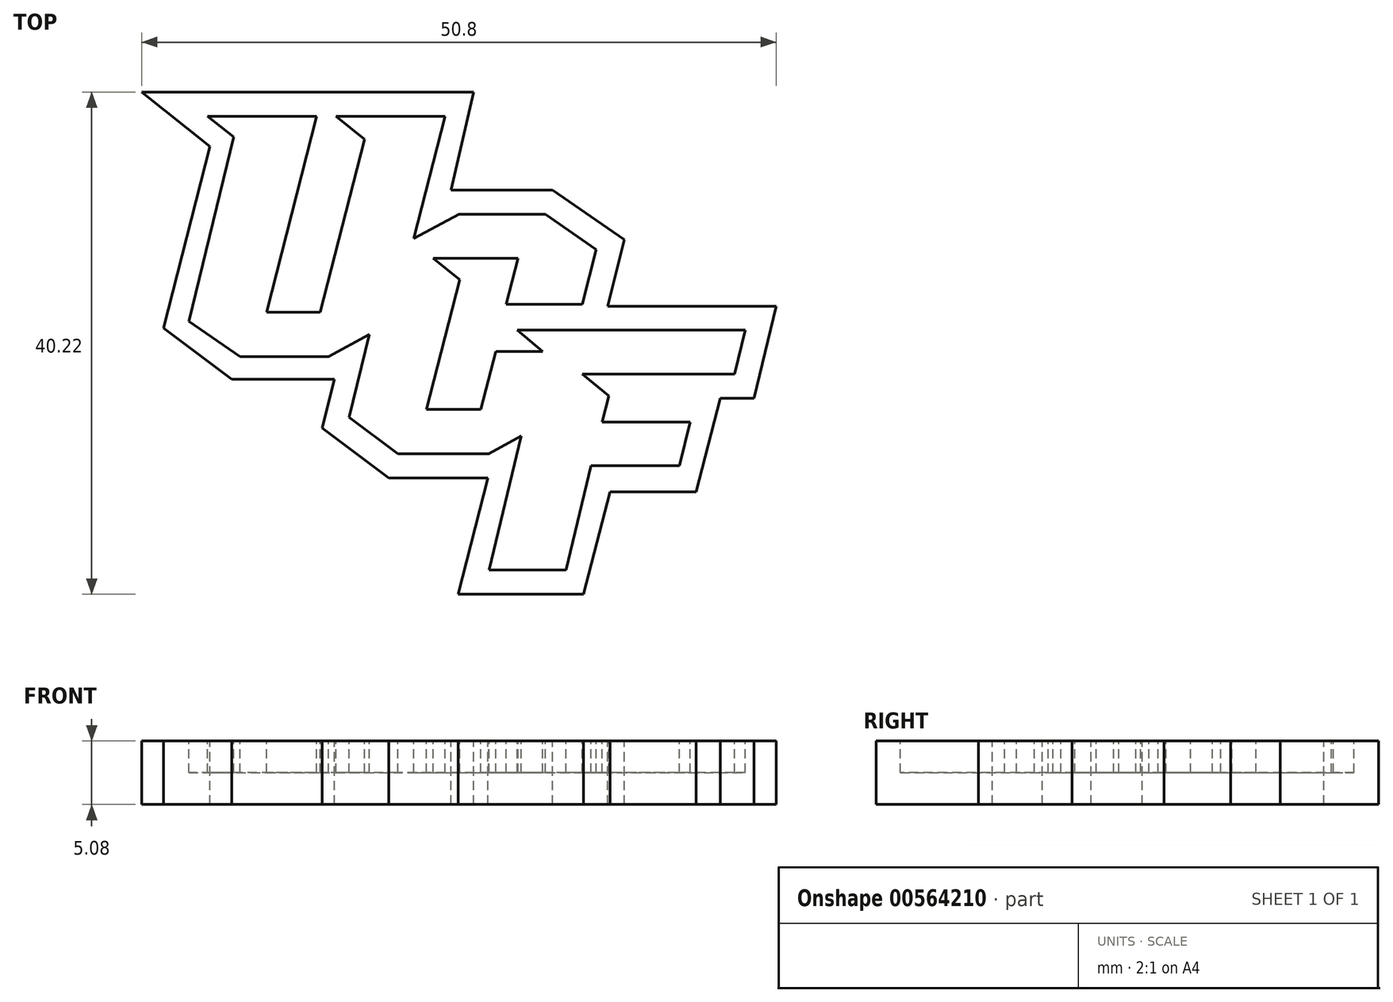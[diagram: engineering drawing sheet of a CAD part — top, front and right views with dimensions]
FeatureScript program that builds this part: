
annotation { "Feature Type Name" : "Feature", "Feature Type Description" : "" }
export const myFeature = defineFeature(function(context is Context, id is Id, definition is map)
    precondition{}
    {
        {
            var Q0;
            Q0=qCreatedBy(makeId("Top.planeOp"),FACE);
            var sketch = newSketch(context, id + "F0", { "sketchPlane" : qUnion([Q0])});
            skLineSegment(sketch, "E0", {"start": v(-24.4, 19.25) * mm, "end": v(2.19, 19.25) * mm});
            skLineSegment(sketch, "E1", {"start": v(2.19, 19.25) * mm, "end": v(0.35, 11.38) * mm});
            skLineSegment(sketch, "E2", {"start": v(0.35, 11.38) * mm, "end": v(8.5, 11.38) * mm});
            skLineSegment(sketch, "E3", {"start": v(8.5, 11.38) * mm, "end": v(14.26, 7.42) * mm});
            skLineSegment(sketch, "E4", {"start": v(14.26, 7.42) * mm, "end": v(12.9, 2.1) * mm});
            skLineSegment(sketch, "E5", {"start": v(12.9, 2.1) * mm, "end": v(26.4, 2.1) * mm});
            skLineSegment(sketch, "E6", {"start": v(26.4, 2.1) * mm, "end": v(24.63, -5.27) * mm});
            skLineSegment(sketch, "E7", {"start": v(24.63, -5.27) * mm, "end": v(21.92, -5.27) * mm});
            skLineSegment(sketch, "E8", {"start": v(21.92, -5.27) * mm, "end": v(20, -12.77) * mm});
            skLineSegment(sketch, "E9", {"start": v(20, -12.77) * mm, "end": v(13.09, -12.77) * mm});
            skLineSegment(sketch, "E10", {"start": v(13.09, -12.77) * mm, "end": v(10.99, -20.97) * mm});
            skLineSegment(sketch, "E11", {"start": v(10.99, -20.97) * mm, "end": v(0.94, -20.97) * mm});
            skLineSegment(sketch, "E12", {"start": v(0.94, -20.97) * mm, "end": v(3.33, -11.66) * mm});
            skLineSegment(sketch, "E13", {"start": v(3.33, -11.66) * mm, "end": v(-4.63, -11.66) * mm});
            skLineSegment(sketch, "E14", {"start": v(-4.63, -11.66) * mm, "end": v(-9.96, -7.66) * mm});
            skLineSegment(sketch, "E15", {"start": v(-9.96, -7.66) * mm, "end": v(-8.96, -3.76) * mm});
            skLineSegment(sketch, "E16", {"start": v(-8.96, -3.76) * mm, "end": v(-17.19, -3.76) * mm});
            skLineSegment(sketch, "E17", {"start": v(-17.19, -3.76) * mm, "end": v(-22.66, 0.35) * mm});
            skLineSegment(sketch, "E18", {"start": v(-22.66, 0.35) * mm, "end": v(-18.94, 14.88) * mm});
            skLineSegment(sketch, "E19", {"start": v(-18.94, 14.88) * mm, "end": v(-24.4, 19.25) * mm});
            skLineSegment(sketch, "E20", {"start": v(-17.04, 15.64) * mm, "end": v(-19.12, 17.3) * mm});
            skLineSegment(sketch, "E21", {"start": v(-19.12, 17.3) * mm, "end": v(-10.38, 17.3) * mm});
            skLineSegment(sketch, "E22", {"start": v(-10.38, 17.3) * mm, "end": v(-14.4, 1.61) * mm});
            skLineSegment(sketch, "E23", {"start": v(-14.4, 1.61) * mm, "end": v(-10.1, 1.61) * mm});
            skLineSegment(sketch, "E24", {"start": v(-10.1, 1.61) * mm, "end": v(-6.55, 15.47) * mm});
            skLineSegment(sketch, "E25", {"start": v(-6.55, 15.47) * mm, "end": v(-8.85, 17.3) * mm});
            skLineSegment(sketch, "E26", {"start": v(-8.85, 17.3) * mm, "end": v(-0.1, 17.3) * mm});
            skLineSegment(sketch, "E27", {"start": v(-0.1, 17.3) * mm, "end": v(-2.61, 7.52) * mm});
            skLineSegment(sketch, "E28", {"start": v(-2.61, 7.52) * mm, "end": v(1.02, 9.45) * mm});
            skLineSegment(sketch, "E29", {"start": v(1.02, 9.45) * mm, "end": v(7.92, 9.45) * mm});
            skLineSegment(sketch, "E30", {"start": v(7.92, 9.45) * mm, "end": v(12, 6.64) * mm});
            skLineSegment(sketch, "E31", {"start": v(12, 6.64) * mm, "end": v(10.87, 2.24) * mm});
            skLineSegment(sketch, "E32", {"start": v(10.87, 2.24) * mm, "end": v(4.77, 2.24) * mm});
            skLineSegment(sketch, "E33", {"start": v(4.77, 2.24) * mm, "end": v(5.72, 5.94) * mm});
            skLineSegment(sketch, "E34", {"start": v(5.72, 5.94) * mm, "end": v(-1.06, 5.94) * mm});
            skLineSegment(sketch, "E35", {"start": v(-1.06, 5.94) * mm, "end": v(1.06, 4.22) * mm});
            skLineSegment(sketch, "E36", {"start": v(1.06, 4.22) * mm, "end": v(-1.6, -6.17) * mm});
            skLineSegment(sketch, "E37", {"start": v(-1.6, -6.17) * mm, "end": v(2.76, -6.17) * mm});
            skLineSegment(sketch, "E38", {"start": v(2.76, -6.17) * mm, "end": v(3.95, -1.52) * mm});
            skLineSegment(sketch, "E39", {"start": v(3.95, -1.52) * mm, "end": v(7.7, -1.52) * mm});
            skLineSegment(sketch, "E40", {"start": v(7.7, -1.52) * mm, "end": v(5.66, 0.2) * mm});
            skLineSegment(sketch, "E41", {"start": v(5.66, 0.2) * mm, "end": v(23.91, 0.2) * mm});
            skLineSegment(sketch, "E42", {"start": v(23.91, 0.2) * mm, "end": v(23.06, -3.34) * mm});
            skLineSegment(sketch, "E43", {"start": v(23.06, -3.34) * mm, "end": v(10.87, -3.34) * mm});
            skLineSegment(sketch, "E44", {"start": v(10.87, -3.34) * mm, "end": v(13, -5.07) * mm});
            skLineSegment(sketch, "E45", {"start": v(13, -5.07) * mm, "end": v(12.48, -7.18) * mm});
            skLineSegment(sketch, "E46", {"start": v(12.48, -7.18) * mm, "end": v(19.51, -7.18) * mm});
            skLineSegment(sketch, "E47", {"start": v(19.51, -7.18) * mm, "end": v(18.67, -10.68) * mm});
            skLineSegment(sketch, "E48", {"start": v(18.67, -10.68) * mm, "end": v(11.58, -10.68) * mm});
            skLineSegment(sketch, "E49", {"start": v(11.58, -10.68) * mm, "end": v(9.57, -19.03) * mm});
            skLineSegment(sketch, "E50", {"start": v(9.57, -19.03) * mm, "end": v(3.4, -19.03) * mm});
            skLineSegment(sketch, "E51", {"start": v(3.4, -19.03) * mm, "end": v(6, -8.3) * mm});
            skLineSegment(sketch, "E52", {"start": v(6, -8.3) * mm, "end": v(3.39, -9.72) * mm});
            skLineSegment(sketch, "E53", {"start": v(3.39, -9.72) * mm, "end": v(-3.9, -9.72) * mm});
            skLineSegment(sketch, "E54", {"start": v(-3.9, -9.72) * mm, "end": v(-7.78, -6.8) * mm});
            skLineSegment(sketch, "E55", {"start": v(-7.78, -6.8) * mm, "end": v(-6.18, -0.17) * mm});
            skLineSegment(sketch, "E56", {"start": v(-6.18, -0.17) * mm, "end": v(-9.43, -1.94) * mm});
            skLineSegment(sketch, "E57", {"start": v(-9.43, -1.94) * mm, "end": v(-16.52, -1.94) * mm});
            skLineSegment(sketch, "E58", {"start": v(-16.52, -1.94) * mm, "end": v(-20.63, 0.89) * mm});
            skLineSegment(sketch, "E59", {"start": v(-20.63, 0.89) * mm, "end": v(-17.04, 15.64) * mm});
            skLineSegment(sketch, "E60", {"start": v(-19.66, 1.34) * mm, "end": v(-16.1, 15.94) * mm});
            skLineSegment(sketch, "E61", {"start": v(-16.1, 15.94) * mm, "end": v(-16.73, 16.44) * mm});
            skLineSegment(sketch, "E62", {"start": v(-16.73, 16.44) * mm, "end": v(-11.47, 16.44) * mm});
            skLineSegment(sketch, "E63", {"start": v(-11.47, 16.44) * mm, "end": v(-11.68, 15.58) * mm});
            skLineSegment(sketch, "E64", {"start": v(-11.68, 15.58) * mm, "end": v(-15.27, 15.58) * mm});
            skLineSegment(sketch, "E65", {"start": v(-15.27, 15.58) * mm, "end": v(-18.9, 0.72) * mm});
            skLineSegment(sketch, "E66", {"start": v(-18.9, 0.72) * mm, "end": v(-19.66, 1.34) * mm});
            skLineSegment(sketch, "E67", {"start": v(-9.5, 0.81) * mm, "end": v(-5.64, 15.85) * mm});
            skLineSegment(sketch, "E68", {"start": v(-5.64, 15.85) * mm, "end": v(-6.5, 16.54) * mm});
            skLineSegment(sketch, "E69", {"start": v(-6.5, 16.54) * mm, "end": v(-1.13, 16.54) * mm});
            skLineSegment(sketch, "E70", {"start": v(-1.13, 16.54) * mm, "end": v(-1.38, 15.56) * mm});
            skLineSegment(sketch, "E71", {"start": v(-1.38, 15.56) * mm, "end": v(-4.91, 15.56) * mm});
            skLineSegment(sketch, "E72", {"start": v(-4.91, 15.56) * mm, "end": v(-8.93, -0.1) * mm});
            skLineSegment(sketch, "E73", {"start": v(-8.93, -0.1) * mm, "end": v(-14.72, -0.1) * mm});
            skLineSegment(sketch, "E74", {"start": v(-14.72, -0.1) * mm, "end": v(-14.48, 0.81) * mm});
            skLineSegment(sketch, "E75", {"start": v(-14.48, 0.81) * mm, "end": v(-9.5, 0.81) * mm});
            skLineSegment(sketch, "E76", {"start": v(-6.84, -6.48) * mm, "end": v(-3.84, 6) * mm});
            skLineSegment(sketch, "E77", {"start": v(-3.84, 6) * mm, "end": v(1.18, 8.67) * mm});
            skLineSegment(sketch, "E78", {"start": v(1.18, 8.67) * mm, "end": v(7.59, 8.67) * mm});
            skLineSegment(sketch, "E79", {"start": v(7.59, 8.67) * mm, "end": v(8.81, 7.82) * mm});
            skLineSegment(sketch, "E80", {"start": v(8.81, 7.82) * mm, "end": v(1.49, 7.82) * mm});
            skLineSegment(sketch, "E81", {"start": v(1.49, 7.82) * mm, "end": v(-2.96, 5.46) * mm});
            skLineSegment(sketch, "E82", {"start": v(-2.96, 5.46) * mm, "end": v(-6, -7.13) * mm});
            skLineSegment(sketch, "E83", {"start": v(-6, -7.13) * mm, "end": v(-6.84, -6.48) * mm});
            skLineSegment(sketch, "E84", {"start": v(6.58, 5.94) * mm, "end": v(7.49, 5.94) * mm});
            skLineSegment(sketch, "E85", {"start": v(7.49, 5.94) * mm, "end": v(6.78, 3) * mm});
            skLineSegment(sketch, "E86", {"start": v(6.78, 3) * mm, "end": v(5.83, 3) * mm});
            skLineSegment(sketch, "E87", {"start": v(5.83, 3) * mm, "end": v(6.58, 5.94) * mm});
            skLineSegment(sketch, "E88", {"start": v(-1.67, -7) * mm, "end": v(3.4, -7) * mm});
            skLineSegment(sketch, "E89", {"start": v(3.4, -7) * mm, "end": v(4.52, -2.33) * mm});
            skLineSegment(sketch, "E90", {"start": v(4.52, -2.33) * mm, "end": v(7.2, -2.33) * mm});
            skLineSegment(sketch, "E91", {"start": v(7.2, -2.33) * mm, "end": v(7, -3.2) * mm});
            skLineSegment(sketch, "E92", {"start": v(7, -3.2) * mm, "end": v(5.23, -3.2) * mm});
            skLineSegment(sketch, "E93", {"start": v(5.23, -3.2) * mm, "end": v(4.11, -7.87) * mm});
            skLineSegment(sketch, "E94", {"start": v(4.11, -7.87) * mm, "end": v(-1.9, -7.87) * mm});
            skLineSegment(sketch, "E95", {"start": v(-1.9, -7.87) * mm, "end": v(-1.67, -7) * mm});
            skLineSegment(sketch, "E96", {"start": v(8.62, -1.17) * mm, "end": v(7.93, -0.7) * mm});
            skLineSegment(sketch, "E97", {"start": v(7.93, -0.7) * mm, "end": v(22.9, -0.7) * mm});
            skLineSegment(sketch, "E98", {"start": v(22.9, -0.7) * mm, "end": v(22.7, -1.52) * mm});
            skLineSegment(sketch, "E99", {"start": v(22.7, -1.52) * mm, "end": v(9.5, -1.52) * mm});
            skLineSegment(sketch, "E100", {"start": v(9.5, -1.52) * mm, "end": v(5.46, -18.24) * mm});
            skLineSegment(sketch, "E101", {"start": v(5.46, -18.24) * mm, "end": v(4.43, -18.24) * mm});
            skLineSegment(sketch, "E102", {"start": v(4.43, -18.24) * mm, "end": v(8.62, -1.17) * mm});
            skLineSegment(sketch, "E103", {"start": v(12.3, -7.95) * mm, "end": v(18.44, -7.95) * mm});
            skLineSegment(sketch, "E104", {"start": v(18.44, -7.95) * mm, "end": v(18.22, -8.86) * mm});
            skLineSegment(sketch, "E105", {"start": v(18.22, -8.86) * mm, "end": v(12.06, -8.86) * mm});
            skLineSegment(sketch, "E106", {"start": v(12.06, -8.86) * mm, "end": v(12.3, -7.95) * mm});
            skLineSegment(sketch, "E107.0", {"start": v(-20.27, 1.02) * mm, "end": v(-16.68, 15.76) * mm});
            skLineSegment(sketch, "E108.0", {"start": v(-14.8, 1.3) * mm, "end": v(-9.85, 1.3) * mm});
            skLineSegment(sketch, "E109.0", {"start": v(-9.85, 1.3) * mm, "end": v(-6.2, 15.59) * mm});
            skLineSegment(sketch, "E110.0", {"start": v(-6.2, 15.59) * mm, "end": v(-7.94, 17) * mm});
            skLineSegment(sketch, "E111.0", {"start": v(-0.51, 17) * mm, "end": v(-3.1, 6.9) * mm});
            skLineSegment(sketch, "E112.0", {"start": v(-3.1, 6.9) * mm, "end": v(1.1, 9.13) * mm});
            skLineSegment(sketch, "E113.0", {"start": v(1.1, 9.13) * mm, "end": v(7.82, 9.13) * mm});
            skLineSegment(sketch, "E114.0", {"start": v(7.82, 9.13) * mm, "end": v(11.63, 6.5) * mm});
            skLineSegment(sketch, "E115.0", {"start": v(11.63, 6.5) * mm, "end": v(10.62, 2.56) * mm});
            skLineSegment(sketch, "E116.0", {"start": v(10.62, 2.56) * mm, "end": v(5.18, 2.56) * mm});
            skLineSegment(sketch, "E117.0", {"start": v(6.13, 6.26) * mm, "end": v(-1.95, 6.26) * mm});
            skLineSegment(sketch, "E118.0", {"start": v(-1.95, 6.26) * mm, "end": v(0.7, 4.1) * mm});
            skLineSegment(sketch, "E119.0", {"start": v(0.7, 4.1) * mm, "end": v(-2, -6.49) * mm});
            skLineSegment(sketch, "E120.0", {"start": v(-5.7, 0.46) * mm, "end": v(-9.52, -1.63) * mm});
            skLineSegment(sketch, "E121.0", {"start": v(-7.42, -6.66) * mm, "end": v(-5.7, 0.46) * mm});
            skLineSegment(sketch, "E122.0", {"start": v(-9.52, -1.63) * mm, "end": v(-16.43, -1.63) * mm});
            skLineSegment(sketch, "E123.0", {"start": v(-2, -6.49) * mm, "end": v(3, -6.49) * mm});
            skLineSegment(sketch, "E124.0", {"start": v(3, -6.49) * mm, "end": v(4.2, -1.84) * mm});
            skLineSegment(sketch, "E125.0", {"start": v(4.2, -1.84) * mm, "end": v(8.45, -1.84) * mm});
            skLineSegment(sketch, "E126.0", {"start": v(8.56, -1.84) * mm, "end": v(6.53, -0.12) * mm});
            skLineSegment(sketch, "E127.0", {"start": v(22.8, -3.02) * mm, "end": v(9.98, -3.02) * mm});
            skLineSegment(sketch, "E128.0", {"start": v(9.98, -3.02) * mm, "end": v(12.63, -5.2) * mm});
            skLineSegment(sketch, "E129.0", {"start": v(12.63, -5.2) * mm, "end": v(12.08, -7.5) * mm});
            skLineSegment(sketch, "E130.0", {"start": v(12.08, -7.5) * mm, "end": v(19.1, -7.5) * mm});
            skLineSegment(sketch, "E131.0", {"start": v(-3.79, -9.4) * mm, "end": v(-7.42, -6.66) * mm});
            skLineSegment(sketch, "E132.0", {"start": v(3.3, -9.4) * mm, "end": v(-3.79, -9.4) * mm});
            skLineSegment(sketch, "E133.0", {"start": v(6.47, -7.68) * mm, "end": v(3.3, -9.4) * mm});
            skLineSegment(sketch, "E134.0", {"start": v(3.81, -18.71) * mm, "end": v(6.47, -7.68) * mm});
            skLineSegment(sketch, "E135.0", {"start": v(-16.43, -1.63) * mm, "end": v(-20.27, 1.02) * mm});
            skLineSegment(sketch, "E136.0", {"start": v(9.32, -18.71) * mm, "end": v(3.81, -18.71) * mm});
            skLineSegment(sketch, "E137.0", {"start": v(11.33, -10.37) * mm, "end": v(9.32, -18.71) * mm});
            skLineSegment(sketch, "E138.0", {"start": v(18.42, -10.37) * mm, "end": v(11.33, -10.37) * mm});
            skLineSegment(sketch, "E139.trimOffspring", {"start": v(-18.21, 17) * mm, "end": v(-10.79, 17) * mm});
            skLineSegment(sketch, "E140", {"start": v(-16.68, 15.76) * mm, "end": v(-18.21, 17) * mm});
            skLineSegment(sketch, "E141.trimOffspring", {"start": v(-10.79, 17) * mm, "end": v(-14.8, 1.3) * mm});
            skLineSegment(sketch, "E142.trimOffspring", {"start": v(-7.94, 17) * mm, "end": v(-0.51, 17) * mm});
            skLineSegment(sketch, "E143.trimOffspring", {"start": v(19.1, -7.5) * mm, "end": v(18.42, -10.37) * mm});
            skLineSegment(sketch, "E144.trimOffspring", {"start": v(23.5, -0.12) * mm, "end": v(22.8, -3.02) * mm});
            skLineSegment(sketch, "E145.trimOffspring", {"start": v(6.53, -0.12) * mm, "end": v(23.5, -0.12) * mm});
            skLineSegment(sketch, "E146.trimOffspring", {"start": v(5.18, 2.56) * mm, "end": v(6.13, 6.26) * mm});
            skSolve(sketch);
        }
        {
            var Q0;
            Q0=makeQuery(id+"F0.imprint","IMPRINT",FACE,{"disambiguationData":[TD([[makeQuery(id+"F0.imprint","IMPRINT",EDGE,{"derivedFrom":sQuery(id+"F0.wireOp",EDGE,"E0")}),-1.0]])]});
            var Q1;
            Q1=makeQuery(id+"F0.imprint","IMPRINT",FACE,{"disambiguationData":[TD([[makeQuery(id+"F0.imprint","IMPRINT",EDGE,{"derivedFrom":sQuery(id+"F0.wireOp",EDGE,"E20")}),-1.0]])]});
            var Q2;
            Q2=makeQuery(id+"F0.imprint","IMPRINT",FACE,{"disambiguationData":[TD([[makeQuery(id+"F0.imprint","IMPRINT",EDGE,{"derivedFrom":sQuery(id+"F0.wireOp",EDGE,"E67")}),-1.0]])]});
            var Q3;
            Q3=makeQuery(id+"F0.imprint","IMPRINT",FACE,{"disambiguationData":[TD([[makeQuery(id+"F0.imprint","IMPRINT",EDGE,{"derivedFrom":sQuery(id+"F0.wireOp",EDGE,"E60")}),-1.0]])]});
            var Q4;
            Q4=makeQuery(id+"F0.imprint","IMPRINT",FACE,{"disambiguationData":[TD([[makeQuery(id+"F0.imprint","IMPRINT",EDGE,{"derivedFrom":sQuery(id+"F0.wireOp",EDGE,"E76")}),-1.0]])]});
            var Q5;
            Q5=makeQuery(id+"F0.imprint","IMPRINT",FACE,{"disambiguationData":[TD([[makeQuery(id+"F0.imprint","IMPRINT",EDGE,{"derivedFrom":sQuery(id+"F0.wireOp",EDGE,"E84")}),-1.0]])]});
            var Q6;
            Q6=makeQuery(id+"F0.imprint","IMPRINT",FACE,{"disambiguationData":[TD([[makeQuery(id+"F0.imprint","IMPRINT",EDGE,{"derivedFrom":sQuery(id+"F0.wireOp",EDGE,"E96")}),-1.0]])]});
            var Q7;
            Q7=makeQuery(id+"F0.imprint","IMPRINT",FACE,{"disambiguationData":[TD([[makeQuery(id+"F0.imprint","IMPRINT",EDGE,{"derivedFrom":sQuery(id+"F0.wireOp",EDGE,"E88")}),-1.0]])]});
            var Q8;
            Q8=makeQuery(id+"F0.imprint","IMPRINT",FACE,{"disambiguationData":[TD([[makeQuery(id+"F0.imprint","IMPRINT",EDGE,{"derivedFrom":sQuery(id+"F0.wireOp",EDGE,"E103")}),-1.0]])]});
            var Q9;
            Q9=makeQuery(id+"F0.imprint","IMPRINT",FACE,{"disambiguationData":[TD([[makeQuery(id+"F0.imprint","IMPRINT",EDGE,{"derivedFrom":sQuery(id+"F0.wireOp",EDGE,"E60")}),1.0]])]});
            var Q10;
            {var subQ0=sQuery(id+"F0.wireOp",EDGE,"E117.0");var subQ1=sQuery(id+"F0.wireOp",EDGE,"E81");var subQ2=makeQuery(id+"F0.imprint","INTERSECT",VERTEX,{"derivedFrom":[subQ1,subQ0]});Q10=makeQuery(id+"F0.imprint","IMPRINT",FACE,{"disambiguationData":[TD([[makeQuery(id+"F0.imprint","IMPRINT",EDGE,{"disambiguationData":[TD([[subQ2,-1.0]])],"derivedFrom":subQ1}),-1.0]])]});}
            extrude(context, id + "F1", {"entities" : qUnion([Q0, Q1, Q2, Q3, Q4, Q5, Q6, Q7, Q8, Q9, Q10]), "depth" : -5.08 * mm, "offsetDistance" : 25.4 * mm});
        }
        {
            var Q0;
            Q0=makeQuery(id+"F0.imprint","IMPRINT",FACE,{"disambiguationData":[TD([[makeQuery(id+"F0.imprint","IMPRINT",EDGE,{"derivedFrom":sQuery(id+"F0.wireOp",EDGE,"E60")}),1.0]])]});
            var Q1;
            Q1=makeQuery(id+"F0.imprint","IMPRINT",FACE,{"disambiguationData":[TD([[makeQuery(id+"F0.imprint","IMPRINT",EDGE,{"derivedFrom":sQuery(id+"F0.wireOp",EDGE,"E20")}),-1.0]])]});
            var Q2;
            Q2=makeQuery(id+"F0.imprint","IMPRINT",FACE,{"disambiguationData":[TD([[makeQuery(id+"F0.imprint","IMPRINT",EDGE,{"derivedFrom":sQuery(id+"F0.wireOp",EDGE,"E67")}),-1.0]])]});
            var Q3;
            Q3=makeQuery(id+"F0.imprint","IMPRINT",FACE,{"disambiguationData":[TD([[makeQuery(id+"F0.imprint","IMPRINT",EDGE,{"derivedFrom":sQuery(id+"F0.wireOp",EDGE,"E60")}),-1.0]])]});
            var Q4;
            Q4=makeQuery(id+"F0.imprint","IMPRINT",FACE,{"disambiguationData":[TD([[makeQuery(id+"F0.imprint","IMPRINT",EDGE,{"derivedFrom":sQuery(id+"F0.wireOp",EDGE,"E76")}),-1.0]])]});
            var Q5;
            Q5=makeQuery(id+"F0.imprint","IMPRINT",FACE,{"disambiguationData":[TD([[makeQuery(id+"F0.imprint","IMPRINT",EDGE,{"derivedFrom":sQuery(id+"F0.wireOp",EDGE,"E84")}),-1.0]])]});
            var Q6;
            {var subQ0=sQuery(id+"F0.wireOp",EDGE,"E117.0");var subQ1=sQuery(id+"F0.wireOp",EDGE,"E81");var subQ2=makeQuery(id+"F0.imprint","INTERSECT",VERTEX,{"derivedFrom":[subQ1,subQ0]});Q6=makeQuery(id+"F0.imprint","IMPRINT",FACE,{"disambiguationData":[TD([[makeQuery(id+"F0.imprint","IMPRINT",EDGE,{"disambiguationData":[TD([[subQ2,-1.0]])],"derivedFrom":subQ1}),-1.0]])]});}
            var Q7;
            Q7=makeQuery(id+"F0.imprint","IMPRINT",FACE,{"disambiguationData":[TD([[makeQuery(id+"F0.imprint","IMPRINT",EDGE,{"derivedFrom":sQuery(id+"F0.wireOp",EDGE,"E88")}),-1.0]])]});
            var Q8;
            {var subQ0=sQuery(id+"F0.wireOp",EDGE,"E96");Q8=makeQuery(id+"F0.imprint","IMPRINT",FACE,{"disambiguationData":[TD([[makeQuery(id+"F0.imprint","IMPRINT",EDGE,{"derivedFrom":subQ0}),-1.0]])]});}
            var Q9;
            Q9=makeQuery(id+"F0.imprint","IMPRINT",FACE,{"disambiguationData":[TD([[makeQuery(id+"F0.imprint","IMPRINT",EDGE,{"derivedFrom":sQuery(id+"F0.wireOp",EDGE,"E103")}),-1.0]])]});
            extrude(context, id + "F2", {"entities" : qUnion([Q0, Q1, Q2, Q3, Q4, Q5, Q6, Q7, Q8, Q9]), "operationType" : NewBodyOperationType.REMOVE, "oppositeDirection" : true, "depth" : 2.54 * mm, "offsetDistance" : 25.4 * mm});
        }
    });
